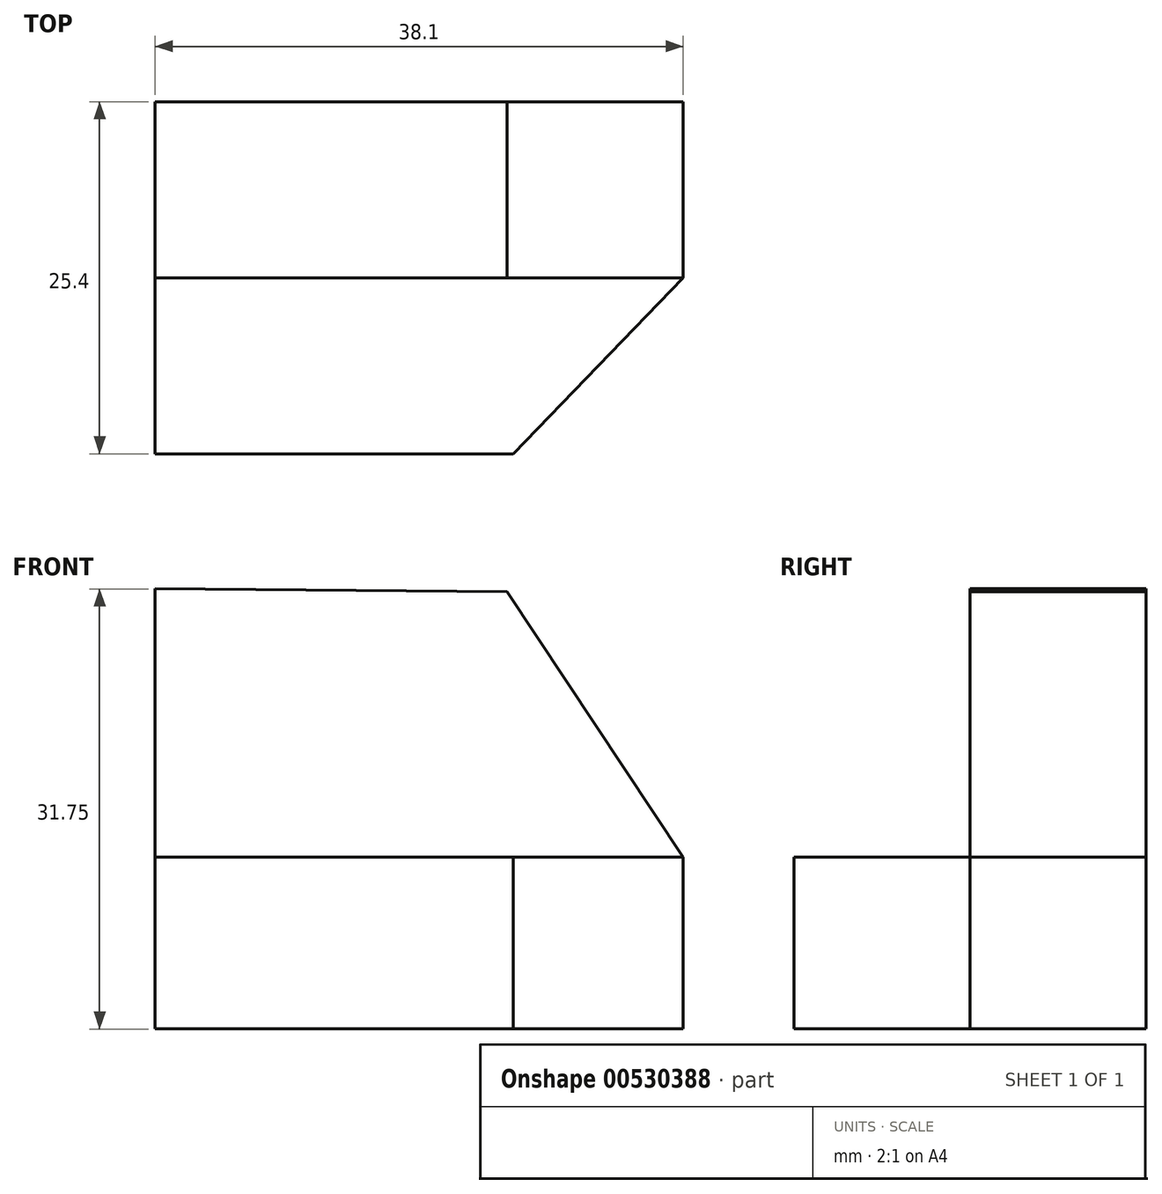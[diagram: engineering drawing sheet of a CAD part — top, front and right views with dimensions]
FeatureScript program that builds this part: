
annotation { "Feature Type Name" : "Feature", "Feature Type Description" : "" }
export const myFeature = defineFeature(function(context is Context, id is Id, definition is map)
    precondition{}
    {
        {
            var Q0;
            Q0=qCreatedBy(makeId("Front.planeOp"),FACE);
            var sketch = newSketch(context, id + "F0", { "sketchPlane" : qUnion([Q0])});
            skLineSegment(sketch, "E0", {"start": v(-31.5, 0.02) * mm, "end": v(6.6, 0.02) * mm});
            skLineSegment(sketch, "E1", {"start": v(6.6, -0.29) * mm, "end": v(6.6, 31.46) * mm});
            skLineSegment(sketch, "E2", {"start": v(-31.5, 0.02) * mm, "end": v(-31.5, 31.77) * mm});
            skLineSegment(sketch, "E3", {"start": v(-31.5, 31.77) * mm, "end": v(6.6, 31.46) * mm});
            skSolve(sketch);
        }
        {
            var Q0;
            Q0 = qSketchRegion(id + "F0", true);
            extrude(context, id + "F1", {"entities" : qUnion([Q0]), "depth" : 25.4 * mm, "offsetDistance" : 25.4 * mm});
        }
        {
            var Q0;
            Q0=makeQuery(id+"F1.opExtrude","SWEPT_FACE",FACE,{"disambiguationData":[OSD([sQuery(id+"F0.wireOp",EDGE,"E1")])]});
            var sketch = newSketch(context, id + "F2", { "sketchPlane" : qUnion([Q0])});
            skLineSegment(sketch, "E4", {"start": v(-25.4, 12.41) * mm, "end": v(-12.7, 12.41) * mm});
            skLineSegment(sketch, "E5", {"start": v(-12.7, 12.41) * mm, "end": v(-12.7, 31.46) * mm});
            skLineSegment(sketch, "E6", {"start": v(-12.7, 31.46) * mm, "end": v(-25.4, 31.46) * mm});
            skLineSegment(sketch, "E7", {"start": v(-25.4, 31.46) * mm, "end": v(-25.4, 12.41) * mm});
            skSolve(sketch);
        }
        {
            var Q0;
            Q0=makeQuery(id+"F2.imprint","IMPRINT",FACE,{"disambiguationData":[TD([[makeQuery(id+"F2.imprint","IMPRINT",EDGE,{"derivedFrom":sQuery(id+"F2.wireOp",EDGE,"E4")}),1.0]])]});
            extrude(context, id + "F3", {"entities" : qUnion([Q0]), "operationType" : NewBodyOperationType.REMOVE, "endBound" : BoundingType.THROUGH_ALL, "oppositeDirection" : true, "depth" : 25.4 * mm, "offsetDistance" : 25.4 * mm});
        }
        {
            var Q0;
            Q0=makeQuery(id+"F1.opExtrude","SWEPT_FACE",FACE,{"disambiguationData":[OSD([sQuery(id+"F0.wireOp",EDGE,"E3")])]});
            var sketch = newSketch(context, id + "F4", { "sketchPlane" : qUnion([Q0])});
            skLineSegment(sketch, "E8", {"start": v(-31.75, -12.7) * mm, "end": v(6.35, -12.7) * mm});
            skLineSegment(sketch, "E9", {"start": v(6.35, -12.7) * mm, "end": v(6.35, -25.4) * mm});
            skLineSegment(sketch, "E10", {"start": v(6.06, -24.48) * mm, "end": v(-31.75, -25.4) * mm});
            skLineSegment(sketch, "E11", {"start": v(-31.75, -12.7) * mm, "end": v(-31.75, -25.4) * mm});
            skSolve(sketch);
        }
        {
            var Q0;
            Q0=makeQuery(id+"F4.imprint","IMPRINT",FACE,{"disambiguationData":[TD([[makeQuery(id+"F4.imprint","IMPRINT",EDGE,{"derivedFrom":sQuery(id+"F4.wireOp",EDGE,"E8")}),-1.0]])]});
            extrude(context, id + "F5", {"entities" : qUnion([Q0]), "operationType" : NewBodyOperationType.REMOVE, "oppositeDirection" : true, "depth" : 2.54 * mm, "offsetDistance" : 25.4 * mm});
        }
        {
            var Q0;
            Q0=makeQuery(id+"F5.boolean.opBoolean","MERGE",FACE,{"derivedFrom":[makeQuery(id+"F3.boolean.opBoolean","COPY",FACE,{"derivedFrom":makeQuery(id+"F3.opExtrude","SWEPT_FACE",FACE,{"disambiguationData":[OSD([sQuery(id+"F2.wireOp",EDGE,"E5")])]})}),makeQuery(id+"F5.opExtrude","SWEPT_FACE",FACE,{"disambiguationData":[OSD([sQuery(id+"F4.wireOp",EDGE,"E8")])]})]});
            var sketch = newSketch(context, id + "F6", { "sketchPlane" : qUnion([Q0])});
            skLineSegment(sketch, "E12", {"start": v(6.6, 12.41) * mm, "end": v(-6.1, 31.57) * mm});
            skLineSegment(sketch, "E13", {"start": v(-6.1, 31.57) * mm, "end": v(6.6, 31.46) * mm});
            skLineSegment(sketch, "E14", {"start": v(6.67, 31.46) * mm, "end": v(6.6, 12.41) * mm});
            skSolve(sketch);
        }
        {
            var Q0;
            Q0=makeQuery(id+"F6.imprint","IMPRINT",FACE,{"disambiguationData":[TD([[makeQuery(id+"F6.imprint","IMPRINT",EDGE,{"derivedFrom":sQuery(id+"F6.wireOp",EDGE,"E12")}),-1.0]])]});
            extrude(context, id + "F7", {"entities" : qUnion([Q0]), "operationType" : NewBodyOperationType.REMOVE, "endBound" : BoundingType.THROUGH_ALL, "oppositeDirection" : true, "depth" : 25.4 * mm, "offsetDistance" : 25.4 * mm});
        }
        {
            var Q0;
            Q0=makeQuery(id+"F3.boolean.opBoolean","COPY",FACE,{"derivedFrom":makeQuery(id+"F3.opExtrude","SWEPT_FACE",FACE,{"disambiguationData":[OSD([sQuery(id+"F2.wireOp",EDGE,"E4")])]})});
            var sketch = newSketch(context, id + "F8", { "sketchPlane" : qUnion([Q0])});
            skLineSegment(sketch, "E15", {"start": v(6.6, -12.7) * mm, "end": v(-5.67, -25.4) * mm});
            skLineSegment(sketch, "E16", {"start": v(-5.67, -25.4) * mm, "end": v(6.6, -25.4) * mm});
            skLineSegment(sketch, "E17", {"start": v(6.6, -25.4) * mm, "end": v(6.6, -12.7) * mm});
            skSolve(sketch);
        }
        {
            var Q0;
            Q0=makeQuery(id+"F8.imprint","IMPRINT",FACE,{"disambiguationData":[TD([[makeQuery(id+"F8.imprint","IMPRINT",EDGE,{"derivedFrom":sQuery(id+"F8.wireOp",EDGE,"E15")}),1.0]])]});
            extrude(context, id + "F9", {"entities" : qUnion([Q0]), "operationType" : NewBodyOperationType.REMOVE, "endBound" : BoundingType.THROUGH_ALL, "oppositeDirection" : true, "depth" : 25.4 * mm, "offsetDistance" : 25.4 * mm});
        }
    });
